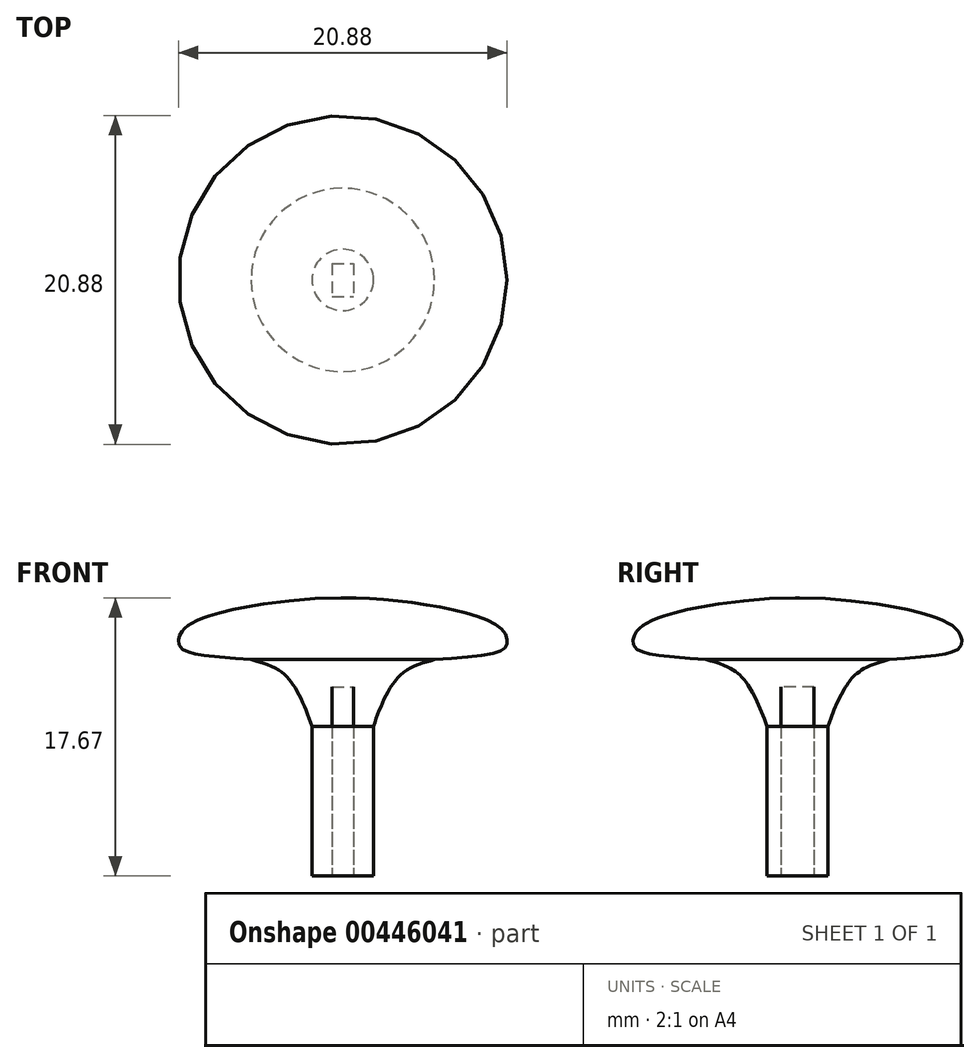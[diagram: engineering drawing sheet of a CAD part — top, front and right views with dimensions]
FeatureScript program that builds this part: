
annotation { "Feature Type Name" : "Feature", "Feature Type Description" : "" }
export const myFeature = defineFeature(function(context is Context, id is Id, definition is map)
    precondition{}
    {
        {
            var Q0;
            Q0=qCreatedBy(makeId("Top.planeOp"),FACE);
            var sketch = newSketch(context, id + "F0", { "sketchPlane" : qUnion([Q0])});
            skCircle(sketch, "E0", {"center": v(0, 0) * mm, "radius": 1.95 * mm});
            skLineSegment(sketch, "E1.bottom", {"start": v(-0.68, 1.05) * mm, "end": v(0.68, 1.05) * mm});
            skLineSegment(sketch, "E1.top", {"start": v(-0.67, -1.05) * mm, "end": v(0.68, -1.05) * mm});
            skLineSegment(sketch, "E1.left", {"start": v(-0.68, 1.05) * mm, "end": v(-0.67, -1.05) * mm});
            skLineSegment(sketch, "E1.right", {"start": v(0.67, 1.05) * mm, "end": v(0.68, -1.05) * mm});
            skSolve(sketch);
        }
        {
            var Q0;
            Q0=qCreatedBy(makeId("Front.planeOp"),FACE);
            var sketch = newSketch(context, id + "F1", { "sketchPlane" : qUnion([Q0])});
            skLineSegment(sketch, "E2", {"start": v(-1.95, 0) * mm, "end": v(1.95, 0) * mm});
            skLineSegment(sketch, "E3", {"start": v(0, 0) * mm, "end": v(0, 13.5) * mm});
            skLineSegment(sketch, "E4", {"start": v(0, 13.5) * mm, "end": v(1.95, 13.5) * mm});
            skLineSegment(sketch, "E5", {"start": v(1.95, 13.5) * mm, "end": v(1.95, 0) * mm});
            skFitSpline(sketch, "E6", {"points": [v(0, 17.67) * mm, v(6.55, 17) * mm, v(10.1, 15.67) * mm, v(10.42, 14.76) * mm, v(9.78, 14.21) * mm, v(1.95, 13.5) * mm], "startDerivative": vector(21.51, 0.12) * mm, "endDerivative": vector(-23.36, -1.73) * mm});
            skLineSegment(sketch, "E7", {"start": v(0, 17.67) * mm, "end": v(0, 13.5) * mm});
            skPoint(sketch, "E8", {"position": v(1.95, 9.5) * mm});
            skFitSpline(sketch, "E9", {"points": [v(1.95, 9.5) * mm, v(3.2, 12.22) * mm, v(5.82, 13.74) * mm], "startDerivative": vector(1.98, 5.94) * mm, "endDerivative": vector(9.2, 2.28) * mm});
            skSolve(sketch);
        }
        {
            var Q0;
            Q0 = qSketchRegion(id + "F1", true);
            var Q1;
            Q1=sQuery(id+"F1.wireOp",EDGE,"E3");
            revolve(context, id + "F2", {"entities" : qUnion([Q0]), "axis" : qUnion([Q1]), "revolveType" : RevolveType.FULL});
        }
        {
            var Q0;
            Q0=makeQuery(id+"F0.imprint","IMPRINT",FACE,{"disambiguationData":[TD([[makeQuery(id+"F0.imprint","IMPRINT",EDGE,{"derivedFrom":sQuery(id+"F0.wireOp",EDGE,"E1.bottom")}),-1.0]])]});
            extrude(context, id + "F3", {"entities" : qUnion([Q0]), "operationType" : NewBodyOperationType.REMOVE, "depth" : 12 * mm});
        }
    });
